# Revit family: dl_11_iq___st1_2a_5xa5575ev14hp00022_13c9
name_source: partatom
category: Lighting Fixtures
units: mm (PartAtom-declared; Revit-internal decimal feet)

## family parameters
Cut with Voids When Loaded = No
Host = Face
Light Source = No
Part Type = Normal
Room Calculation Point = No
Round Connector Dimension = Use Diameter
Shared = No

## types (1)
- --- (1 x LED, 4790 lm, 33.5 W, 3000K)
    Apparent Load = 34 VA
    CIE Flux Codes = 23 60 93 95 100
    Color Rendering = 70
    Color Temperature = 3000K
    Default Elevation = 1800 mm
    Description = DL 11 iQ, mast luminaire, Module 540 iQ-SR, primary light control with 3 zone facetted reflector, of plastic, silver coated, highly specular, structured, primary optical cover: cover, of PMMA, transparent, light distribution: ST1.2a, light emission: direct distribution, primary light characteristic: asymmetric, installation type: post-top, LED, High Power LED, rated luminous flux: 4.790lm, luminous efficacy: 143lm/W, light colour: 730, colour temperature: 3000K, control gear: iQ-Street Remote, D4i with power reduction, control: pre-setting: logarithmic dimming characteristic, Street-Remote, Auto-Match, Temp-Guard, Lumen-Switch, Night-Set, Smart-Wire, Light-Fading, Desk-Remote (wireless, voltage-free reading and setting of iQ features in the workshop via application-optimized NFC function/RFID function), optimised constant luminous flux control (CLO 2.0), mains connection: 220..240V, AC, 50/60Hz, connection cable pre-assembled, cable length: 5,5m, start of lifetime: 34W, end of service life: 36W, reduction: 15W, luminaire housing, upper part, of diecast aluminium, coated, Siteco® metallic grey (DB 702S), spigot size: 76mm (post-top), mounting height: 3..5m, post-top mast mounting element, of diecast aluminium, coated, Siteco® metallic grey (DB 702S), Module 540 iQ-SR, traffic white (RAL 9016), equipment: Power, Smart Interface above, protection rating (complete): IP66, insulation class (complete): insulation class II (safety insulation), certification: CE, ENEC, ENEC+, VDE, impact resistance: IK07, packaging unit: 1 piece

Light Distribution: ST1.2a
    Height = 665 mm
    Lamp = 1 x LED
    Lamp Light Flux = 4790 lm
    Lamp Power = 33.5 W
    Lamp count = 1
    Length = 334 mm
    Luminous efficacy = 143 lm/W
    Manufacturer = Siteco
    ModVariant = No
    Model = 5XA5575EV14HP00022
    Number of Poles = 1
    OnlyDefault = Yes
    Power Factor = 1
    Product Name = DL 11 iQ | ST1.2a
    Product group = mast luminaire | pylon top
    ProductGroupID = 6100
    Protection Class = Protection class II
    Protection Degree = IP 66
    RLX_Detail_Level = 1
    RLX_Emergency_Light_Flux = 0 lm
    RLX_Emergency_Type = 0
    RLX_Emergency_Type_DB = No
    RlxData = <blob elided: 146073 chars, md5=3d5a1232>
    Socket = socket
    Standby Power = 0 W
    System Light Flux = 4790 lm
    System Power = 34 W
    Type Comments = factory setting: luminous flux: 100 % | dim-lin: 254 | 695 mA
    Type Image = l_1337541.jpg
    URL = http://relux.com
    VarID = @adj_053861
    Voltage = 0 V
    Weight = 0.00 kg
    Width = 0 mm  [stored 0 ft]

note: [stored X ft] marks values corroborated as IEEE doubles in the binary element streams (Revit-internal decimal feet)

## geometry (parser evidence)
native form markers: Sweep x8
no freeform markers — native parametric forms only
